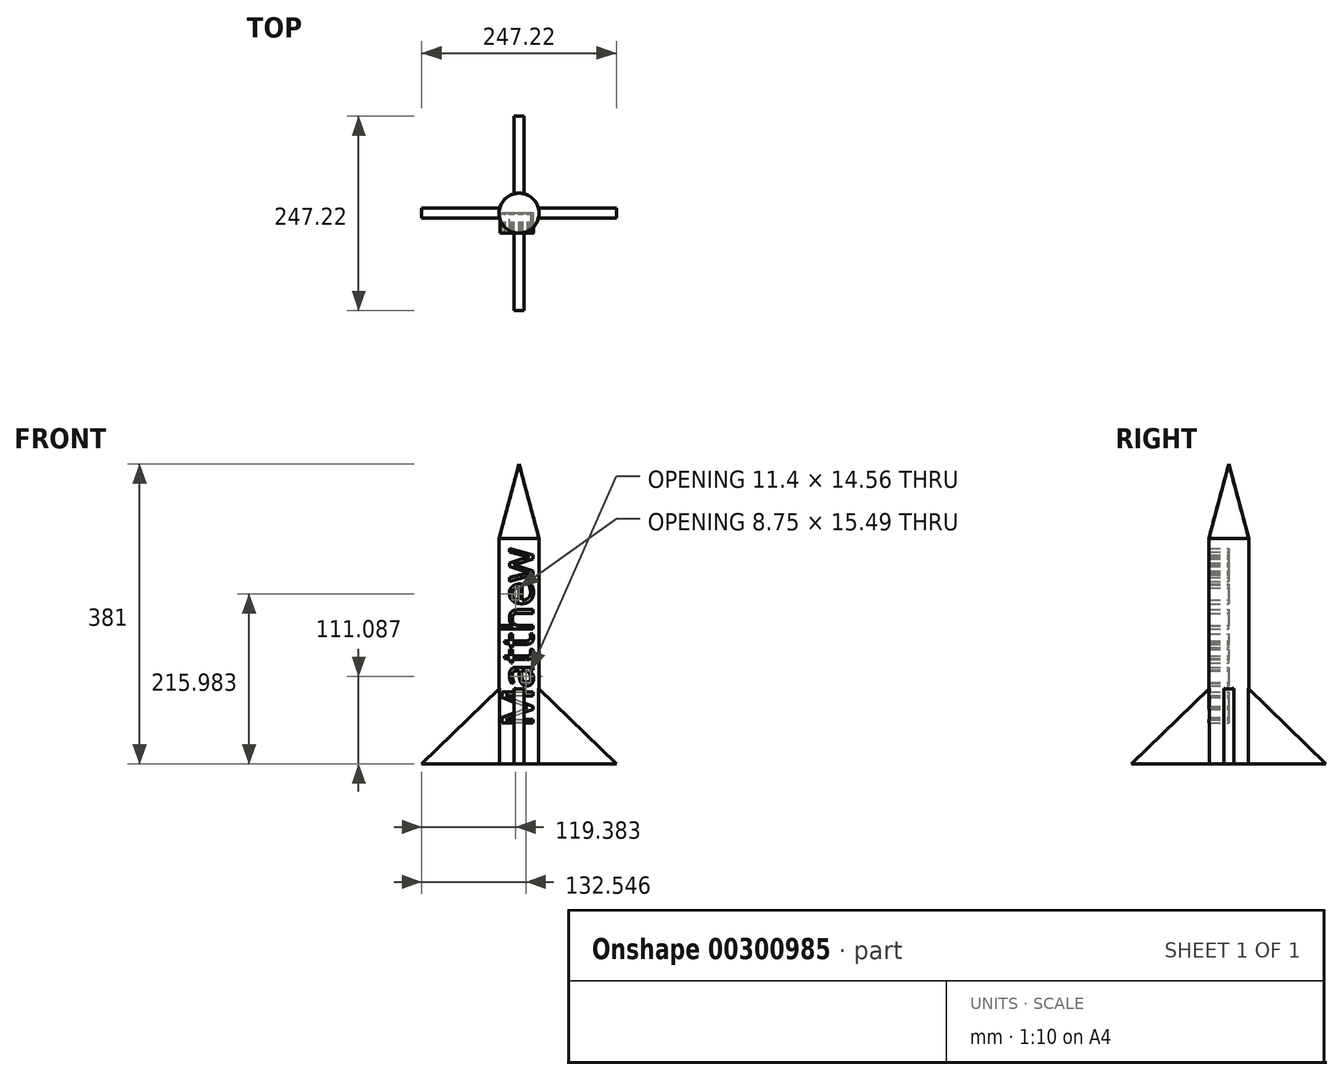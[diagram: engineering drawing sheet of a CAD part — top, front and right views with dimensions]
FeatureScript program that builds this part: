
annotation { "Feature Type Name" : "Feature", "Feature Type Description" : "" }
export const myFeature = defineFeature(function(context is Context, id is Id, definition is map)
    precondition{}
    {
        {
            var Q0;
            Q0=qCreatedBy(makeId("Top.planeOp"),FACE);
            var sketch = newSketch(context, id + "F0", { "sketchPlane" : qUnion([Q0])});
            skCircle(sketch, "E0", {"center": v(0, 0) * mm, "radius": 25.4 * mm});
            skSolve(sketch);
        }
        {
            var Q0;
            Q0=makeQuery(id+"F0.imprint","IMPRINT",FACE,{"disambiguationData":[TD([[makeQuery(id+"F0.imprint","IMPRINT",EDGE,{"derivedFrom":sQuery(id+"F0.wireOp",EDGE,"E0")}),1.0]])]});
            var Q1;
            Q1=sQuery(id+"F0.wireOp",EDGE,"E0");
            extrude(context, id + "F1", {"entities" : qUnion([Q0]), "surfaceEntities" : qUnion([Q1]), "depth" : 381 * mm});
        }
        {
            var Q0;
            Q0=makeQuery(id+"F1.opExtrude","CAP_EDGE",EDGE,{"disambiguationData":[OSD([sQuery(id+"F0.wireOp",EDGE,"E0")])],"isStart":false});
            chamfer(context, id + "F2", {"entities" : qUnion([Q0]), "chamferType" : ChamferType.OFFSET_ANGLE, "width" : 25.4 * mm, "oppositeDirection" : false, "angle" : 75 * degree, "tangentPropagation" : true});
        }
        {
            var Q0;
            Q0=qCreatedBy(makeId("Front.planeOp"),FACE);
            var sketch = newSketch(context, id + "F3", { "sketchPlane" : qUnion([Q0])});
            skLineSegment(sketch, "E1", {"start": v(0, 0) * mm, "end": v(0, 119.82) * mm});
            skLineSegment(sketch, "E2", {"start": v(0, 119.82) * mm, "end": v(123.6, 0) * mm});
            skLineSegment(sketch, "E3", {"start": v(123.6, 0) * mm, "end": v(0, 0) * mm});
            skSolve(sketch);
        }
        {
            var Q0;
            Q0 = qSketchRegion(id + "F3", true);
            extrude(context, id + "F4", {"entities" : qUnion([Q0]), "operationType" : NewBodyOperationType.ADD, "endBound" : BoundingType.SYMMETRIC, "depth" : 12.7 * mm});
        }
        {
            var Q0;
            Q0=makeQuery(id+"F1.opExtrude","SWEPT_BODY",BODY,{"disambiguationData":[OSD([sQuery(id+"F0.wireOp",EDGE,"E0")])]});
            var Q1;
            Q1=makeQuery(id+"F1.opExtrude","SWEPT_FACE",FACE,{"disambiguationData":[OSD([sQuery(id+"F0.wireOp",EDGE,"E0")])]});
            circularPattern(context, id + "F5", {"entities" : qUnion([Q0]), "axis" : qUnion([Q1]), "angle" : 360 * degree, "instanceCount" : 4, "equalSpace" : true});
        }
        {
            var Q0;
            Q0=qCreatedBy(makeId("Front.planeOp"),FACE);
            var sketch = newSketch(context, id + "F6", { "sketchPlane" : qUnion([Q0])});
            skText(sketch, "E4", { "text": "Matthew\n", "fontName": "OpenSans-Regular.ttf"});
            const initialGuessF6  = {"E4": [0.0178, 0.04659, 0, 1, 0.03985]};
            skSetInitialGuess(sketch, initialGuessF6);
            skSolve(sketch);
        }
        {
            var Q0;
            Q0=qCreatedBy(makeId("Top.planeOp"),FACE);
            var sketch = newSketch(context, id + "F7", { "sketchPlane" : qUnion([Q0])});
            skCircle(sketch, "E5", {"center": v(0, 0) * mm, "radius": 35.5 * mm});
            skSolve(sketch);
        }
        {
            var Q0;
            Q0=sQuery(id+"F7.wireOp",EDGE,"E5");
            extrude(context, id + "F8", {"bodyType" : ToolBodyType.SURFACE, "surfaceEntities" : qUnion([Q0]), "depth" : 25.4 * mm});
        }
        {
            var Q0;
            Q0 = qSketchRegion(id + "F6", true);
            var Q1;
            Q1 = qConstructionFilter(qBodyType(qCreatedBy(id + "F6" ,EDGE), BodyType.WIRE), ConstructionObject.NO);
            extrude(context, id + "F9", {"entities" : qUnion([Q0]), "surfaceEntities" : qUnion([Q1]), "depth" : 25.4 * mm});
        }
    });
